# Revit family: IEK_Выключатель_Встраиваемый_С Инд 10А двухклавишный IP20_КВАРТА
name_source: partatom
category: Выключатели
units: mm (PartAtom-declared; Revit-internal decimal feet)

## family parameters
Всегда вертикально = Да
На основе рабочей плоскости = Нет
Общий = Нет
При загрузке вырезать с полостями = Нет
Размер круглого соединителя = Использовать диаметр
Сохранять ориентацию аннотаций = Да
Тип детали = Переключатель
Точка расчета площади = Нет

## types (2) — shared parameters
ADSK_URL страницы изделия = https://www.iek.ru
ADSK_Версия Revit = 2019
ADSK_Версия семейства = 1.0
ADSK_Группирование = III ЭЛЕКТРОУСТАНОВОЧНЫЕ И ЭЛЕКТРОМОНТАЖНЫЕ ИЗДЕЛИЯ
ADSK_Единица измерения = шт
ADSK_Завод-изготовитель = IEK
ADSK_Количество фаз = 1
ADSK_Количество фаз числовое = 1
ADSK_Марка = КВАРТА
ADSK_Масса = 0.099
ADSK_Материал наименование = Пластик
ADSK_Напряжение = 220 В
IEK_URL = https://www.iek.ru
IEK_Описание = Классический дизайн, проверенный временем и востребованный различными категориями потребителей, позволяет устанавливать изделия серии "КВАРТА" в квартирах, загородных домах, офисных и производственных помещениях.
KSI_CMa_Строительные материалы = 01.7.14.03
KSI_CPr_Строительные изделия = 20.4.01
Высота = 81 мм
Глубина = 46 мм
Изготовитель = IEK
Степень защиты = IP20
Тип монтажа = Скрытый монтаж (в штукатурку)
Ширина = 82 мм

## per-type parameters (varying)
| type | ADSK_Код изделия | ADSK_Материал | ADSK_Наименование | IEK_Цена за единицу |
| ВС10-2-1-КБ | EVK21-K01-10-DM | Цвет белый | Выключатель 2-клавишный с индикацией ВС10-2-1-КБ 10А КВАРТА белый IEK | 158.42 |
| ВС10-2-1-ККм | EVK21-K33-10-DM | Цвет кремовый | Выключатель 2-клавишный с индикацией ВС10-2-1-ККм 10А КВАРТА кремовый IEK | 151.87 |
